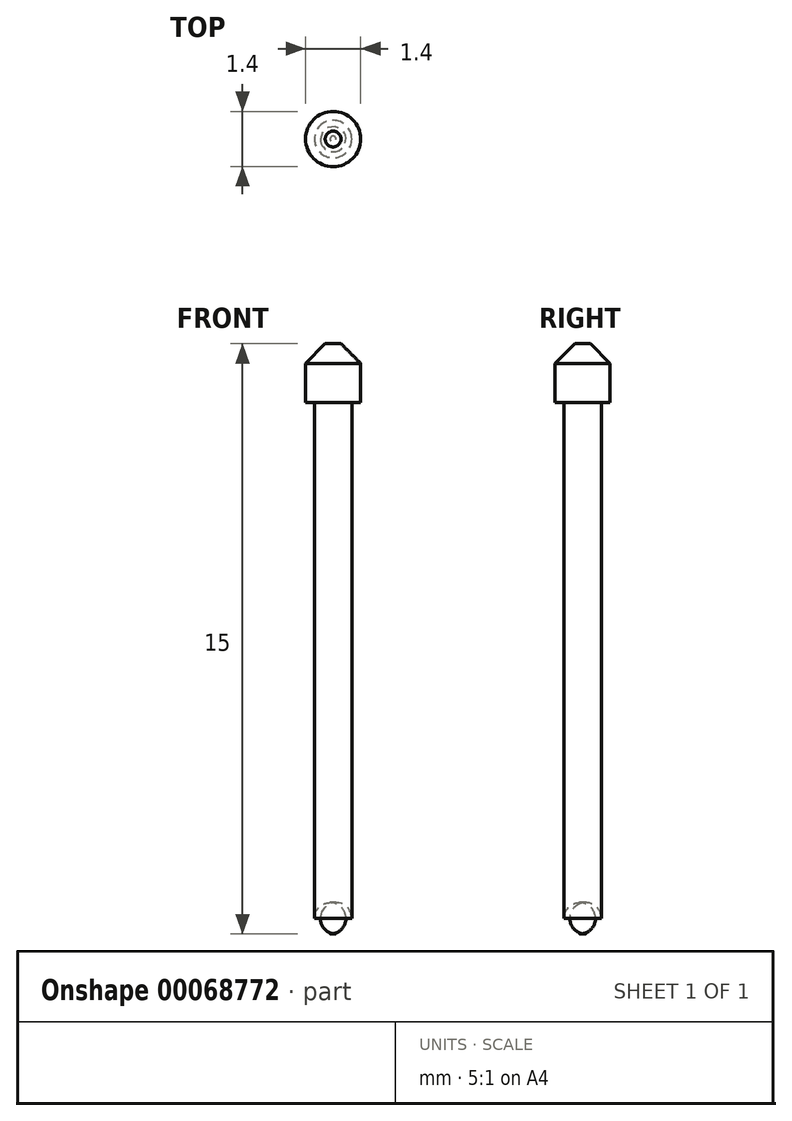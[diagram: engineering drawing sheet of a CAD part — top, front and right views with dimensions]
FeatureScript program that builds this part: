
annotation { "Feature Type Name" : "Feature", "Feature Type Description" : "" }
export const myFeature = defineFeature(function(context is Context, id is Id, definition is map)
    precondition{}
    {
        {
            var Q0;
            Q0=qCreatedBy(makeId("Top.planeOp"),FACE);
            var sketch = newSketch(context, id + "F0", { "sketchPlane" : qUnion([Q0])});
            skCircle(sketch, "E0", {"center": v(0, 0) * mm, "radius": 0.48 * mm});
            skCircle(sketch, "E1", {"center": v(0, 0) * mm, "radius": 0.7 * mm});
            skSolve(sketch);
        }
        {
            var Q0;
            Q0=makeQuery(id+"F0.imprint","IMPRINT",FACE,{"disambiguationData":[TD([[makeQuery(id+"F0.imprint","IMPRINT",EDGE,{"derivedFrom":sQuery(id+"F0.wireOp",EDGE,"E0")}),1.0]])]});
            extrude(context, id + "F1", {"entities" : qUnion([Q0]), "depth" : 15 * mm});
        }
        {
            var Q0;
            Q0 = qSketchRegion(id + "F0", true);
            extrude(context, id + "F2", {"entities" : qUnion([Q0]), "operationType" : NewBodyOperationType.ADD, "depth" : 15 * mm, "hasSecondDirection" : true, "secondDirectionOppositeDirection" : false, "secondDirectionDepth" : 13.5 * mm});
        }
        {
            var Q0;
            Q0=makeQuery(id+"F2.opExtrude","CAP_EDGE",EDGE,{"disambiguationData":[OSD([sQuery(id+"F0.wireOp",EDGE,"E1")])],"isStart":false});
            chamfer(context, id + "F3", {"entities" : qUnion([Q0]), "width" : 0.5 * mm, "tangentPropagation" : true});
        }
        {
            var Q0;
            Q0=makeQuery(id+"F1.opExtrude","CAP_EDGE",EDGE,{"disambiguationData":[OSD([sQuery(id+"F0.wireOp",EDGE,"E0")])],"isStart":true});
            fillet(context, id + "F4", {"entities" : qUnion([Q0]), "radius" : 0.4 * mm, "tangentPropagation" : true, "allowEdgeOverflow" : false});
        }
    });
